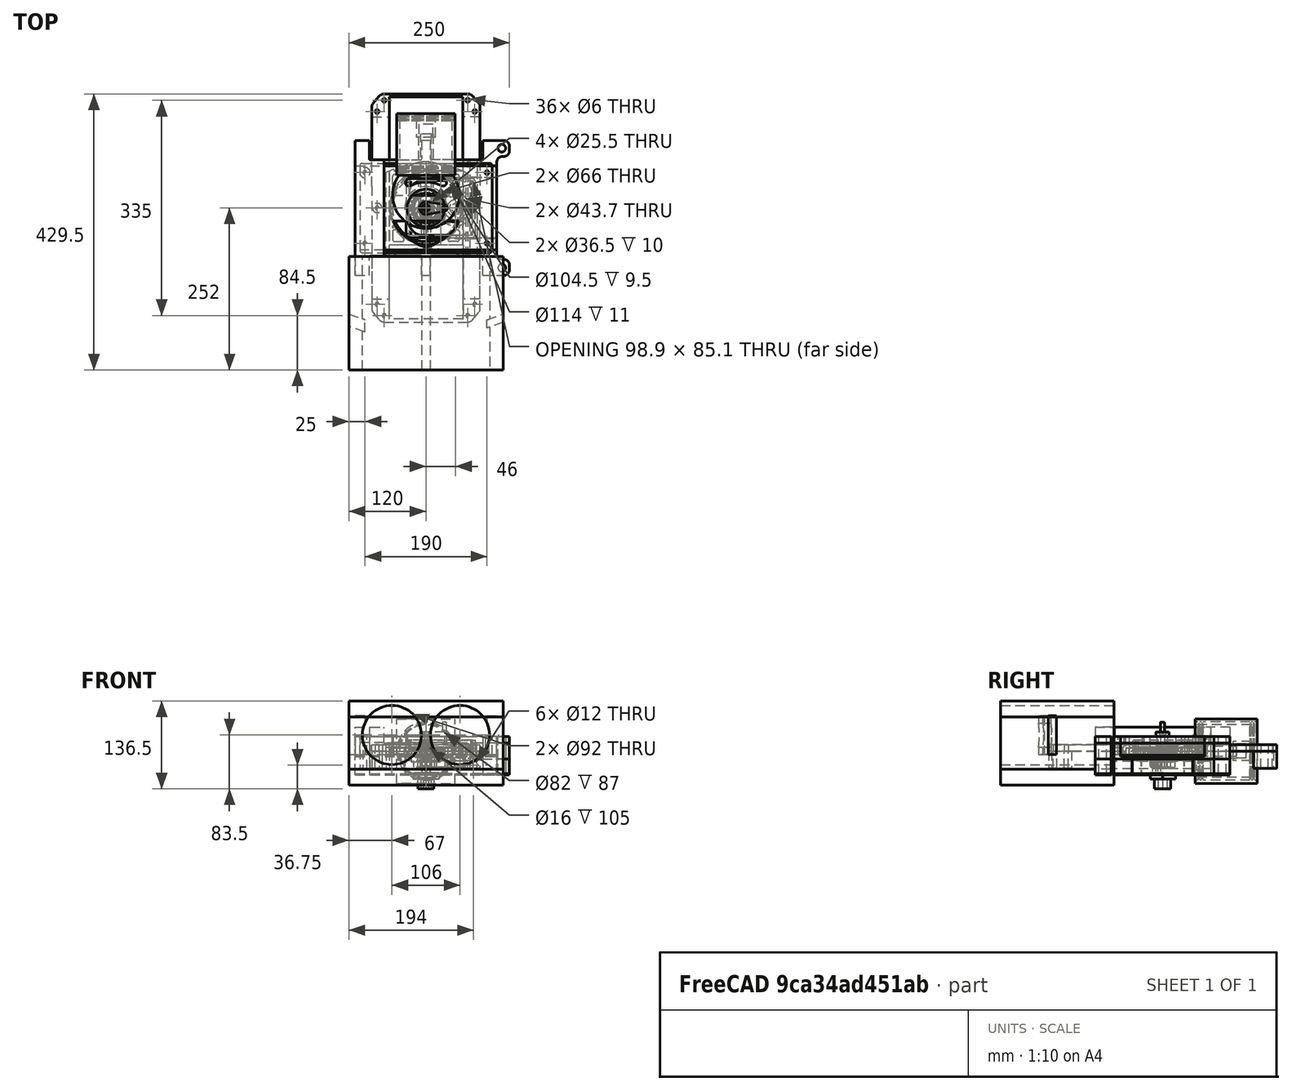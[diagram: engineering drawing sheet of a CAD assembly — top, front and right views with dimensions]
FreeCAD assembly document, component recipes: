
FREECAD ASSEMBLY — COMPONENT RECIPES ("assm4_Paired_at_Tusi_engine")

This assembly document has 39 components, labeled P0..P38 below (a component is one placed body or linked part). 38 of them carry a construction recipe — the FreeCAD feature program that regenerates the part from scratch, quoted from this document or its linked companion documents; the rest are supplied as boundary geometry only. No exploded tour is included for this assembly.
NOTE — document 2 of 2 of this assembly tour. The two overview renders and the header above are repeated from document 1; the component sections below continue where the previous document stopped.
COMPONENT P36 — recipe-attached ("проставка_корпуса_с_шестернями", modeled in this document).
Construction recipe (the document's own serialized feature program — sketch geometry with constraints, then the solid features built on it; lengths are millimeters unless a unit is written):

FEATURE [Sketcher::SketchObject] Sketch075
  FullyConstrained = true
  MapMode = 5
  Support = -> [XY_Plane096]
  expr: Constraints[14] = <<Dim_table>>.inter_shaft_len * 2.15
  expr: Constraints[15] = <<Dim_table>>.ecc_dia * 1.2
  expr: Constraints[16] = <<Dim_table>>.inter_shaft_len * 1.85
  expr: Constraints[22] = <<Dim_table>>.inter_shaft_len / 2
  expr: Constraints[37] = <<Dim_table>>.inter_shaft_len * 2.35
  expr: Constraints[38] = <<Dim_table>>.crank_dia2
  expr: Constraints[39] = <<Dim_table>>.inter_shaft_len * 2
  expr: Constraints[45] = <<Dim_table>>.inter_shaft_len / 2
  expr: Constraints[53] = <<Dim_table>>.axle_hole_dia
  expr: Constraints[56] = <<Dim_table>>.inter_shaft_len
  expr: Constraints[58] = <<Dim_table>>.inter_shaft_len * 0.95
  sketch-geometry (26):
    g0: LineSegment StartX=-4.85 StartY=-42.55 StartZ=0 EndX=50.85 EndY=-42.55 EndZ=0
    g1: LineSegment StartX=72.45 StartY=-20.95 StartZ=0 EndX=72.45 EndY=20.95 EndZ=0
    g2: LineSegment StartX=50.85 StartY=42.55 StartZ=0 EndX=-4.85 EndY=42.55 EndZ=0
    g3: LineSegment StartX=-26.45 StartY=20.95 StartZ=0 EndX=-26.45 EndY=-20.95 EndZ=0
    g4: ArcOfCircle CenterX=-4.85 CenterY=20.95 CenterZ=0 NormalX=0 NormalY=0 NormalZ=1 AngleXU=0 Radius=21.6 StartAngle=1.5708 EndAngle=3.14159
    g5: ArcOfCircle CenterX=50.85 CenterY=20.95 CenterZ=0 NormalX=0 NormalY=0 NormalZ=1 AngleXU=0 Radius=21.6 StartAngle=0 EndAngle=1.5708
    g6: ArcOfCircle CenterX=-4.85 CenterY=-20.95 CenterZ=0 NormalX=0 NormalY=0 NormalZ=1 AngleXU=0 Radius=21.6 StartAngle=3.14159 EndAngle=4.71239
    g7: ArcOfCircle CenterX=50.85 CenterY=-20.95 CenterZ=0 NormalX=0 NormalY=0 NormalZ=1 AngleXU=0 Radius=21.6 StartAngle=4.71239 EndAngle=6.28319
    g8: LineSegment StartX=-26.45 StartY=-20.95 StartZ=0 EndX=72.45 EndY=20.95 EndZ=0
    g9: GeomPoint X=23 Y=0 Z=0
    g10: ArcOfCircle CenterX=-24.8 CenterY=39.75 CenterZ=0 NormalX=0 NormalY=0 NormalZ=1 AngleXU=0 Radius=6.25 StartAngle=1.5708 EndAngle=3.14159
    g11: LineSegment StartX=70.8 StartY=46 StartZ=0 EndX=-24.8 EndY=46 EndZ=0
    g12: ArcOfCircle CenterX=70.8 CenterY=39.75 CenterZ=0 NormalX=0 NormalY=0 NormalZ=1 AngleXU=0 Radius=6.25 StartAngle=0 EndAngle=1.5708
    g13: LineSegment StartX=77.05 StartY=-39.75 StartZ=0 EndX=77.05 EndY=39.75 EndZ=0
    g14: ArcOfCircle CenterX=70.8 CenterY=-39.75 CenterZ=0 NormalX=0 NormalY=0 NormalZ=1 AngleXU=0 Radius=6.25 StartAngle=4.71239 EndAngle=6.28319
    g15: LineSegment StartX=-24.8 StartY=-46 StartZ=0 EndX=70.8 EndY=-46 EndZ=0
    g16: ArcOfCircle CenterX=-24.8 CenterY=-39.75 CenterZ=0 NormalX=0 NormalY=0 NormalZ=1 AngleXU=0 Radius=6.25 StartAngle=3.14159 EndAngle=4.71239
    g17: LineSegment StartX=-31.05 StartY=39.75 StartZ=0 EndX=-31.05 EndY=-39.75 EndZ=0
    g18: LineSegment StartX=-24.8 StartY=46 StartZ=0 EndX=70.8 EndY=-46 EndZ=0
    g19: GeomPoint X=23 Y=0 Z=0
    g20: Circle CenterX=-24.8 CenterY=39.75 CenterZ=0 NormalX=0 NormalY=0 NormalZ=1 AngleXU=0 Radius=1.5
    g21: Circle CenterX=70.8 CenterY=39.75 CenterZ=0 NormalX=0 NormalY=0 NormalZ=1 AngleXU=0 Radius=1.5
    g22: Circle CenterX=-24.8 CenterY=-39.75 CenterZ=0 NormalX=0 NormalY=0 NormalZ=1 AngleXU=0 Radius=1.5
    g23: Circle CenterX=70.8 CenterY=-39.75 CenterZ=0 NormalX=0 NormalY=0 NormalZ=1 AngleXU=0 Radius=1.5
    g24: Circle CenterX=0 CenterY=0 CenterZ=0 NormalX=0 NormalY=0 NormalZ=1 AngleXU=0 Radius=21.85
    g25: Circle CenterX=46 CenterY=0 CenterZ=0 NormalX=0 NormalY=0 NormalZ=1 AngleXU=0 Radius=21.85
  constraints (59):
    c: Horizontal(g0)
    c: Horizontal(g2)
    c: Vertical(g1)
    c: Vertical(g3)
    c: Tangent(g2,g4) = -1.5708
    c: Tangent(g3,g4) = -1.5708
    c: Tangent(g2,g5) = -1.5708
    c: Tangent(g1,g5) = -1.5708
    c: Tangent(g3,g6) = -1.5708
    c: Tangent(g0,g6) = -1.5708
    c: Tangent(g0,g7) = -1.5708
    c: Tangent(g1,g7) = -1.5708
    c: Equal(g4,g5)
    c: Equal(g5,g7)
    c: DistanceX(g3,g1) = 98.9
    c: Diameter(g4) = 43.2
    c: DistanceY(g0,g2) = 85.1
    c: Symmetric(g2,g0,g-1)
    c: Coincident(g8,g3)
    c: Coincident(g8,g1)
    c: PointOnObject(g9,g-1)
    c: PointOnObject(g9,g8)
    c: DistanceX(g-1,g9) = 23
    c: Horizontal(g15)
    c: Horizontal(g11)
    c: Vertical(g13)
    c: Vertical(g17)
    c: Tangent(g11,g10) = -1.5708
    c: Tangent(g17,g10) = -1.5708
    c: Tangent(g11,g12) = -1.5708
    c: Tangent(g13,g12) = -1.5708
    c: Tangent(g17,g16) = -1.5708
    c: Tangent(g15,g16) = -1.5708
    c: Tangent(g15,g14) = -1.5708
    c: Tangent(g13,g14) = -1.5708
    c: Equal(g10,g12)
    c: Equal(g12,g14)
    c: DistanceX(g17,g13) = 108.1
    c: Diameter(g10) = 12.5
    c: DistanceY(g15,g11) = 92
    c: Symmetric(g10,g16,g-1)
    c: Coincident(g18,g10)
    c: Coincident(g18,g14)
    c: PointOnObject(g19,g-1)
    c: PointOnObject(g19,g18)
    c: DistanceX(g-1,g19) = 23
    c: Coincident(g20,g10)
    c: Coincident(g21,g12)
    c: Coincident(g22,g16)
    c: Coincident(g23,g14)
    c: Equal(g22,g23)
    c: Equal(g23,g21)
    c: Equal(g21,g20)
    c: Diameter(g20) = 3
    c: Coincident(g24,g-1)
    c: PointOnObject(g25,g-1)
    c: DistanceX(g24,g25) = 46
    c: Equal(g25,g24)
    c: Diameter(g24) = 43.7
FEATURE [Sketcher::SketchObject] Sketch076
  FullyConstrained = true
  MapMode = 5
  Support = -> [XY_Plane096]
  expr: Constraints[14] = <<Dim_table>>.inter_shaft_len * 2.15
  expr: Constraints[15] = <<Dim_table>>.ecc_dia * 1.2
  expr: Constraints[16] = <<Dim_table>>.inter_shaft_len * 1.85
  expr: Constraints[22] = <<Dim_table>>.inter_shaft_len / 2
  expr: Constraints[37] = <<Dim_table>>.inter_shaft_len * 2.35
  expr: Constraints[38] = <<Dim_table>>.crank_dia2
  expr: Constraints[39] = <<Dim_table>>.inter_shaft_len * 2
  expr: Constraints[45] = <<Dim_table>>.inter_shaft_len / 2
  expr: Constraints[53] = <<Dim_table>>.axle_hole_dia
  sketch-geometry (24):
    g0: LineSegment StartX=-4.85 StartY=-42.55 StartZ=0 EndX=50.85 EndY=-42.55 EndZ=0
    g1: LineSegment StartX=72.45 StartY=-20.95 StartZ=0 EndX=72.45 EndY=20.95 EndZ=0
    g2: LineSegment StartX=50.85 StartY=42.55 StartZ=0 EndX=-4.85 EndY=42.55 EndZ=0
    g3: LineSegment StartX=-26.45 StartY=20.95 StartZ=0 EndX=-26.45 EndY=-20.95 EndZ=0
    g4: ArcOfCircle CenterX=-4.85 CenterY=20.95 CenterZ=0 NormalX=0 NormalY=0 NormalZ=1 AngleXU=0 Radius=21.6 StartAngle=1.5708 EndAngle=3.14159
    g5: ArcOfCircle CenterX=50.85 CenterY=20.95 CenterZ=0 NormalX=0 NormalY=0 NormalZ=1 AngleXU=0 Radius=21.6 StartAngle=0 EndAngle=1.5708
    g6: ArcOfCircle CenterX=-4.85 CenterY=-20.95 CenterZ=0 NormalX=0 NormalY=0 NormalZ=1 AngleXU=0 Radius=21.6 StartAngle=3.14159 EndAngle=4.71239
    g7: ArcOfCircle CenterX=50.85 CenterY=-20.95 CenterZ=0 NormalX=0 NormalY=0 NormalZ=1 AngleXU=0 Radius=21.6 StartAngle=4.71239 EndAngle=6.28319
    g8: LineSegment StartX=-26.45 StartY=-20.95 StartZ=0 EndX=72.45 EndY=20.95 EndZ=0
    g9: GeomPoint X=23 Y=0 Z=0
    g10: ArcOfCircle CenterX=-24.8 CenterY=39.75 CenterZ=0 NormalX=0 NormalY=0 NormalZ=1 AngleXU=0 Radius=6.25 StartAngle=1.5708 EndAngle=3.14159
    g11: LineSegment StartX=70.8 StartY=46 StartZ=0 EndX=-24.8 EndY=46 EndZ=0
    g12: ArcOfCircle CenterX=70.8 CenterY=39.75 CenterZ=0 NormalX=0 NormalY=0 NormalZ=1 AngleXU=0 Radius=6.25 StartAngle=0 EndAngle=1.5708
    g13: LineSegment StartX=77.05 StartY=-39.75 StartZ=0 EndX=77.05 EndY=39.75 EndZ=0
    g14: ArcOfCircle CenterX=70.8 CenterY=-39.75 CenterZ=0 NormalX=0 NormalY=0 NormalZ=1 AngleXU=0 Radius=6.25 StartAngle=4.71239 EndAngle=6.28319
    g15: LineSegment StartX=-24.8 StartY=-46 StartZ=0 EndX=70.8 EndY=-46 EndZ=0
    g16: ArcOfCircle CenterX=-24.8 CenterY=-39.75 CenterZ=0 NormalX=0 NormalY=0 NormalZ=1 AngleXU=0 Radius=6.25 StartAngle=3.14159 EndAngle=4.71239
    g17: LineSegment StartX=-31.05 StartY=39.75 StartZ=0 EndX=-31.05 EndY=-39.75 EndZ=0
    g18: LineSegment StartX=-24.8 StartY=46 StartZ=0 EndX=70.8 EndY=-46 EndZ=0
    g19: GeomPoint X=23 Y=0 Z=0
    g20: Circle CenterX=-24.8 CenterY=39.75 CenterZ=0 NormalX=0 NormalY=0 NormalZ=1 AngleXU=0 Radius=1.5
    g21: Circle CenterX=70.8 CenterY=39.75 CenterZ=0 NormalX=0 NormalY=0 NormalZ=1 AngleXU=0 Radius=1.5
    g22: Circle CenterX=-24.8 CenterY=-39.75 CenterZ=0 NormalX=0 NormalY=0 NormalZ=1 AngleXU=0 Radius=1.5
    g23: Circle CenterX=70.8 CenterY=-39.75 CenterZ=0 NormalX=0 NormalY=0 NormalZ=1 AngleXU=0 Radius=1.5
  constraints (54):
    c: Horizontal(g0)
    c: Horizontal(g2)
    c: Vertical(g1)
    c: Vertical(g3)
    c: Tangent(g2,g4) = -1.5708
    c: Tangent(g3,g4) = -1.5708
    c: Tangent(g2,g5) = -1.5708
    c: Tangent(g1,g5) = -1.5708
    c: Tangent(g3,g6) = -1.5708
    c: Tangent(g0,g6) = -1.5708
    c: Tangent(g0,g7) = -1.5708
    c: Tangent(g1,g7) = -1.5708
    c: Equal(g4,g5)
    c: Equal(g5,g7)
    c: DistanceX(g3,g1) = 98.9
    c: Diameter(g4) = 43.2
    c: DistanceY(g0,g2) = 85.1
    c: Symmetric(g2,g0,g-1)
    c: Coincident(g8,g3)
    c: Coincident(g8,g1)
    c: PointOnObject(g9,g-1)
    c: PointOnObject(g9,g8)
    c: DistanceX(g-1,g9) = 23
    c: Horizontal(g15)
    c: Horizontal(g11)
    c: Vertical(g13)
    c: Vertical(g17)
    c: Tangent(g11,g10) = -1.5708
    c: Tangent(g17,g10) = -1.5708
    c: Tangent(g11,g12) = -1.5708
    c: Tangent(g13,g12) = -1.5708
    c: Tangent(g17,g16) = -1.5708
    c: Tangent(g15,g16) = -1.5708
    c: Tangent(g15,g14) = -1.5708
    c: Tangent(g13,g14) = -1.5708
    c: Equal(g10,g12)
    c: Equal(g12,g14)
    c: DistanceX(g17,g13) = 108.1
    c: Diameter(g10) = 12.5
    c: DistanceY(g15,g11) = 92
    c: Symmetric(g10,g16,g-1)
    c: Coincident(g18,g10)
    c: Coincident(g18,g14)
    c: PointOnObject(g19,g-1)
    c: PointOnObject(g19,g18)
    c: DistanceX(g-1,g19) = 23
    c: Coincident(g20,g10)
    c: Coincident(g21,g12)
    c: Coincident(g22,g16)
    c: Coincident(g23,g14)
    c: Equal(g22,g23)
    c: Equal(g23,g21)
    c: Equal(g21,g20)
    c: Diameter(g20) = 3
FEATURE [PartDesign::CoordinateSystem] LCS_Origin007
  AttacherType = Attacher::AttachEngine3D
  MapMode = 2
  Support = -> [X_Axis094]
FEATURE [PartDesign::Pad] Pad044
  Direction = (0,0,1)
  Length = 6
  Length2 = 10
  Profile = -> Sketch075
  ReferenceAxis = -> Sketch075 [N_Axis]
  Type = 0
FEATURE [PartDesign::Pad] Pad045
  BaseFeature = -> Pad044
  Direction = (0,0,1)
  Length = 16.75
  Length2 = 10
  Profile = -> Sketch076
  ReferenceAxis = -> Sketch076 [N_Axis]
  Type = 0
FEATURE [PartDesign::Body] Body_2  label="проставка_корпуса_с_шестернями"
  Group = -> [LCS_Origin007,Sketch075,Pad044,Sketch076,Pad045]
  Origin = -> Origin095
  Tip = -> Pad045
COMPONENT P37 — recipe-attached ("направляющая_нижнего ползуна", modeled in this document).
Construction recipe (the document's own serialized feature program — sketch geometry with constraints, then the solid features built on it; lengths are millimeters unless a unit is written):

FEATURE [Sketcher::SketchObject] Sketch065
  FullyConstrained = false
  MapMode = 5
  Support = -> [XY_Plane083]
  expr: Constraints[34] = <<assm4_Main_BSM_M3_r80>>#<<Dim_table>>.inter_shaft_len
  expr: Constraints[80] = <<assm4_Main_BSM_M3_r80>>#<<Dim_table>>.ecc_dia + 10 + 0.5
  sketch-geometry (37):
    g0: LineSegment StartX=-84 StartY=-33.8723 StartZ=0 EndX=84 EndY=-33.8723 EndZ=0
    g1: LineSegment StartX=84 StartY=-33.8723 StartZ=0 EndX=84 EndY=33.8723 EndZ=0
    g2: LineSegment StartX=84 StartY=33.8723 StartZ=0 EndX=-84 EndY=33.8723 EndZ=0
    g3: LineSegment StartX=-84 StartY=33.8723 StartZ=0 EndX=-84 EndY=-33.8723 EndZ=0
    g4: LineSegment StartX=-84 StartY=33.8723 StartZ=0 EndX=-84 EndY=159.195 EndZ=0
    g5: LineSegment StartX=84 StartY=159.195 StartZ=0 EndX=84 EndY=33.8723 EndZ=0
    g6: ArcOfCircle CenterX=-80 CenterY=159.195 CenterZ=0 NormalX=0 NormalY=0 NormalZ=1 AngleXU=0 Radius=4 StartAngle=2.43396 EndAngle=3.14159
    g7: ArcOfCircle CenterX=80 CenterY=159.195 CenterZ=0 NormalX=0 NormalY=0 NormalZ=1 AngleXU=0 Radius=4 StartAngle=-2.7e-13 EndAngle=0.707637
    g8: LineSegment StartX=-84 StartY=-33.8723 StartZ=0 EndX=-84 EndY=-159.195 EndZ=0
    g9: LineSegment StartX=84 StartY=-159.195 StartZ=0 EndX=84 EndY=-33.8723 EndZ=0
    g10: Circle CenterX=-76 CenterY=150 CenterZ=0 NormalX=0 NormalY=0 NormalZ=1 AngleXU=0 Radius=3
    g11: Circle CenterX=76 CenterY=150 CenterZ=0 NormalX=0 NormalY=0 NormalZ=1 AngleXU=0 Radius=3
    g12: Circle CenterX=-76 CenterY=-150 CenterZ=0 NormalX=0 NormalY=0 NormalZ=1 AngleXU=0 Radius=3
    g13: Circle CenterX=76 CenterY=-150 CenterZ=0 NormalX=0 NormalY=0 NormalZ=1 AngleXU=0 Radius=3
    g14: Circle CenterX=76 CenterY=0 CenterZ=0 NormalX=0 NormalY=0 NormalZ=1 AngleXU=0 Radius=3
    g15: Circle CenterX=-76 CenterY=0 CenterZ=0 NormalX=0 NormalY=0 NormalZ=1 AngleXU=0 Radius=3
    g16: LineSegment StartX=-65 StartY=177.5 StartZ=0 EndX=65 EndY=177.5 EndZ=0
    g17: LineSegment StartX=72.599 StartY=174 StartZ=0 EndX=83.0396 EndY=161.795 EndZ=0
    g18: LineSegment StartX=-83.0396 StartY=161.795 StartZ=0 EndX=-72.599 EndY=174 EndZ=0
    g19: ArcOfCircle CenterX=-65 CenterY=167.5 CenterZ=0 NormalX=0 NormalY=0 NormalZ=1 AngleXU=0 Radius=10 StartAngle=1.5708 EndAngle=2.43396
    g20: ArcOfCircle CenterX=65 CenterY=167.5 CenterZ=0 NormalX=0 NormalY=0 NormalZ=1 AngleXU=0 Radius=10 StartAngle=0.707637 EndAngle=1.5708
    g21: ArcOfCircle CenterX=-80 CenterY=-159.195 CenterZ=0 NormalX=0 NormalY=0 NormalZ=1 AngleXU=0 Radius=4 StartAngle=3.14159 EndAngle=3.84923
    g22: ArcOfCircle CenterX=80 CenterY=-159.195 CenterZ=0 NormalX=0 NormalY=0 NormalZ=1 AngleXU=0 Radius=4 StartAngle=5.57555 EndAngle=6.28319
    g23: LineSegment StartX=-65 StartY=-177.5 StartZ=0 EndX=65 EndY=-177.5 EndZ=0
    g24: LineSegment StartX=72.599 StartY=-174 StartZ=0 EndX=83.0396 EndY=-161.795 EndZ=0
    g25: LineSegment StartX=-83.0396 StartY=-161.795 StartZ=0 EndX=-72.599 EndY=-174 EndZ=0
    g26: ArcOfCircle CenterX=-65 CenterY=-167.5 CenterZ=0 NormalX=0 NormalY=0 NormalZ=1 AngleXU=0 Radius=10 StartAngle=3.84923 EndAngle=4.71239
    g27: ArcOfCircle CenterX=65 CenterY=-167.5 CenterZ=0 NormalX=0 NormalY=0 NormalZ=1 AngleXU=0 Radius=10 StartAngle=4.71239 EndAngle=5.57555
    g28: Circle CenterX=-65 CenterY=167.5 CenterZ=0 NormalX=0 NormalY=0 NormalZ=1 AngleXU=0 Radius=3
    g29: Circle CenterX=65 CenterY=167.5 CenterZ=0 NormalX=0 NormalY=0 NormalZ=1 AngleXU=0 Radius=3
    g30: Circle CenterX=-65 CenterY=-167.5 CenterZ=0 NormalX=0 NormalY=0 NormalZ=1 AngleXU=0 Radius=3
    g31: Circle CenterX=65 CenterY=-167.5 CenterZ=0 NormalX=0 NormalY=0 NormalZ=1 AngleXU=0 Radius=3
    g32: LineSegment StartX=57.25 StartY=-172.5 StartZ=0 EndX=-57.25 EndY=-172.5 EndZ=0
    g33: LineSegment StartX=-57.25 StartY=-172.5 StartZ=0 EndX=-57.25 EndY=172.5 EndZ=0
    g34: LineSegment StartX=-57.25 StartY=172.5 StartZ=0 EndX=57.25 EndY=172.5 EndZ=0
    g35: LineSegment StartX=57.25 StartY=172.5 StartZ=0 EndX=57.25 EndY=-172.5 EndZ=0
    g36: LineSegment StartX=57.25 StartY=-172.5 StartZ=0 EndX=-57.25 EndY=172.5 EndZ=0
  constraints (82):
    c: Coincident(g0,g1)
    c: Coincident(g1,g2)
    c: Coincident(g2,g3)
    c: Coincident(g3,g0)
    c: Horizontal(g0)
    c: Vertical(g1)
    c: Symmetric(g2,g1,g-2)
    c: Symmetric(g2,g0,g-1)
    c: DistanceX(g2,g2) = 168
    c: Coincident(g4,g3)
    c: Coincident(g5,g1)
    c: Tangent(g4,g6) = 1.5708
    c: Tangent(g5,g7) = 1.5708
    c: Vertical(g4)
    c: Vertical(g5)
    c: Symmetric(g6,g7,g-2)
    c: Radius(g7) = 4
    c: Vertical(g8)
    c: Coincident(g8,g3)
    c: Coincident(g9,g1)
    c: Vertical(g9)
    c: Equal(g10,g11)
    c: Equal(g11,g13)
    c: Equal(g13,g12)
    c: Diameter(g11) = 6
    c: Symmetric(g10,g11,g-2)
    c: Symmetric(g12,g13,g-2)
    c: Symmetric(g12,g10,g-1)
    c: DistanceX(g3,g10) = 8
    c: Equal(g15,g14)
    c: Symmetric(g15,g14,g-2)
    c: PointOnObject(g14,g-1)
    c: DistanceX(g12,g15) = 0
    c: Equal(g15,g10)
    c: DistanceY(g15,g10) = 150
    c: Horizontal(g16)
    c: Tangent(g6,g18) = 1.5708
    c: Tangent(g18,g19) = 1.5708
    c: Tangent(g16,g19) = 1.5708
    c: Tangent(g16,g20) = 1.5708
    c: Tangent(g17,g20) = 1.5708
    c: Tangent(g17,g7) = 1.5708
    c: Symmetric(g19,g20,g-2)
    c: Radius(g22) = 4
    c: Horizontal(g23)
    c: Tangent(g21,g25) = -1.5708
    c: Tangent(g25,g26) = -1.5708
    c: Tangent(g23,g26) = -1.5708
    c: Tangent(g23,g27) = -1.5708
    c: Tangent(g24,g27) = -1.5708
    c: Tangent(g24,g22) = -1.5708
    c: Equal(g25,g18)
    c: Symmetric(g26,g27,g-2)
    c: Equal(g26,g19)
    c: Tangent(g21,g8) = -1.5708
    c: Tangent(g22,g9) = -1.5708
    c: Symmetric(g21,g22,g-2)
    c: DistanceY(g23,g16) = 355
    c: Coincident(g28,g19)
    c: Coincident(g29,g20)
    c: Equal(g28,g29)
    c: Equal(g29,g10)
    c: Equal(g30,g31)
    c: Coincident(g30,g26)
    c: Coincident(g31,g27)
    c: Equal(g31,g13)
    c: DistanceX(g26,g27) = 130
    c: DistanceY(g27,g20) = 335
    c: Symmetric(g16,g23,g-1)
    c: Coincident(g32,g33)
    c: Coincident(g33,g34)
    c: Coincident(g34,g35)
    c: Coincident(g35,g32)
    c: Horizontal(g32)
    c: Horizontal(g34)
    c: Vertical(g33)
    c: Vertical(g35)
    c: Coincident(g36,g32)
    c: Coincident(g36,g33)
    c: Symmetric(g32,g33,g-1)
    c: Distance(g34) = 114.5
    c: DistanceY(g34,g16) = 5
FEATURE [PartDesign::CoordinateSystem] LCS_Origin005
  AttacherType = Attacher::AttachEngine3D
  MapMode = 2
  Support = -> [X_Axis081]
FEATURE [PartDesign::Pad] Pad035
  Direction = (0,0,1)
  Length = 10
  Length2 = 10
  Profile = -> Sketch065
  ReferenceAxis = -> Sketch065 [N_Axis]
  Type = 0
FEATURE [Sketcher::SketchObject] Sketch068
  ExternalGeometry = -> [Pad035]
  FullyConstrained = true
  MapMode = 5
  Placement = pos=(0,-172.5,0) rot=(0,0.707107,0.707107;3.14159rad)
  Support = -> [Pad035]
  sketch-geometry (4):
    g0: ArcOfCircle CenterX=-37.8851 CenterY=5 CenterZ=0 NormalX=0 NormalY=0 NormalZ=1 AngleXU=0 Radius=20 StartAngle=2.88891 EndAngle=3.39427
    g1: ArcOfCircle CenterX=37.8851 CenterY=5 CenterZ=0 NormalX=0 NormalY=0 NormalZ=1 AngleXU=0 Radius=20 StartAngle=6.03051 EndAngle=6.53587
    g2: LineSegment StartX=-57.25 StartY=10 StartZ=0 EndX=-57.25 EndY=1.8296e-12 EndZ=0
    g3: LineSegment StartX=57.25 StartY=10 StartZ=0 EndX=57.25 EndY=1.8243e-12 EndZ=0
  constraints (10):
    c: Coincident(g0,g-3)
    c: Coincident(g0,g-3)
    c: Coincident(g1,g-4)
    c: Coincident(g1,g-4)
    c: Equal(g0,g1)
    c: Radius(g1) = 20
    c: Coincident(g2,g0)
    c: Coincident(g2,g0)
    c: Coincident(g3,g1)
    c: Coincident(g3,g1)
FEATURE [PartDesign::Pocket] Pocket035
  BaseFeature = -> Pad035
  Direction = (0,-1,2e-16)
  Length = 345
  Length2 = 5
  Profile = -> Sketch068
  ReferenceAxis = -> Sketch068 [N_Axis]
  Reversed = true
  Type = 0
FEATURE [PartDesign::Body] ________________________  label="направляющая_нижнего ползуна"
  Group = -> [LCS_Origin005,Sketch065,Pad035,Sketch068,Pocket035]
  Origin = -> Origin082
  Tip = -> Pocket035
COMPONENT P38 — recipe-attached ("корпус_верхний", modeled in this document).
Construction recipe (the document's own serialized feature program — sketch geometry with constraints, then the solid features built on it; lengths are millimeters unless a unit is written):

FEATURE [Sketcher::SketchObject] Sketch067
  FullyConstrained = true
  MapMode = 5
  Support = -> [XY_Plane085]
  expr: Constraints[14] = <<Dim_table>>.inter_shaft_len * 2.15
  expr: Constraints[15] = <<Dim_table>>.ecc_dia * 1.2
  expr: Constraints[16] = <<Dim_table>>.inter_shaft_len * 1.85
  expr: Constraints[22] = <<Dim_table>>.inter_shaft_len / 2
  expr: Constraints[37] = <<Dim_table>>.inter_shaft_len * 2.35
  expr: Constraints[38] = <<Dim_table>>.crank_dia2
  expr: Constraints[39] = <<Dim_table>>.inter_shaft_len * 2
  expr: Constraints[45] = <<Dim_table>>.inter_shaft_len / 2
  expr: Constraints[53] = <<Dim_table>>.axle_hole_dia
  expr: Constraints[56] = <<Dim_table>>.inter_shaft_len
  expr: Constraints[58] = <<Dim_table>>.crank_dia2 + <<Dim_table>>.zazor
  sketch-geometry (27):
    g0: LineSegment StartX=-4.85 StartY=-42.55 StartZ=0 EndX=50.85 EndY=-42.55 EndZ=0
    g1: LineSegment StartX=72.45 StartY=-20.95 StartZ=0 EndX=72.45 EndY=20.95 EndZ=0
    g2: LineSegment StartX=50.85 StartY=42.55 StartZ=0 EndX=-4.85 EndY=42.55 EndZ=0
    g3: LineSegment StartX=-26.45 StartY=20.95 StartZ=0 EndX=-26.45 EndY=-20.95 EndZ=0
    g4: ArcOfCircle CenterX=-4.85 CenterY=20.95 CenterZ=0 NormalX=0 NormalY=0 NormalZ=1 AngleXU=0 Radius=21.6 StartAngle=1.5708 EndAngle=3.14159
    g5: ArcOfCircle CenterX=50.85 CenterY=20.95 CenterZ=0 NormalX=0 NormalY=0 NormalZ=1 AngleXU=0 Radius=21.6 StartAngle=0 EndAngle=1.5708
    g6: ArcOfCircle CenterX=-4.85 CenterY=-20.95 CenterZ=0 NormalX=0 NormalY=0 NormalZ=1 AngleXU=0 Radius=21.6 StartAngle=3.14159 EndAngle=4.71239
    g7: ArcOfCircle CenterX=50.85 CenterY=-20.95 CenterZ=0 NormalX=0 NormalY=0 NormalZ=1 AngleXU=0 Radius=21.6 StartAngle=4.71239 EndAngle=6.28319
    g8: LineSegment StartX=-26.45 StartY=-20.95 StartZ=0 EndX=72.45 EndY=20.95 EndZ=0
    g9: GeomPoint X=23 Y=0 Z=0
    g10: ArcOfCircle CenterX=-24.8 CenterY=39.75 CenterZ=0 NormalX=0 NormalY=0 NormalZ=1 AngleXU=0 Radius=6.25 StartAngle=1.5708 EndAngle=3.14159
    g11: LineSegment StartX=70.8 StartY=46 StartZ=0 EndX=-24.8 EndY=46 EndZ=0
    g12: ArcOfCircle CenterX=70.8 CenterY=39.75 CenterZ=0 NormalX=0 NormalY=0 NormalZ=1 AngleXU=0 Radius=6.25 StartAngle=0 EndAngle=1.5708
    g13: LineSegment StartX=77.05 StartY=-39.75 StartZ=0 EndX=77.05 EndY=39.75 EndZ=0
    g14: ArcOfCircle CenterX=70.8 CenterY=-39.75 CenterZ=0 NormalX=0 NormalY=0 NormalZ=1 AngleXU=0 Radius=6.25 StartAngle=4.71239 EndAngle=6.28319
    g15: LineSegment StartX=-24.8 StartY=-46 StartZ=0 EndX=70.8 EndY=-46 EndZ=0
    g16: ArcOfCircle CenterX=-24.8 CenterY=-39.75 CenterZ=0 NormalX=0 NormalY=0 NormalZ=1 AngleXU=0 Radius=6.25 StartAngle=3.14159 EndAngle=4.71239
    g17: LineSegment StartX=-31.05 StartY=39.75 StartZ=0 EndX=-31.05 EndY=-39.75 EndZ=0
    g18: LineSegment StartX=-24.8 StartY=46 StartZ=0 EndX=70.8 EndY=-46 EndZ=0
    g19: GeomPoint X=23 Y=0 Z=0
    g20: Circle CenterX=-24.8 CenterY=39.75 CenterZ=0 NormalX=0 NormalY=0 NormalZ=1 AngleXU=0 Radius=1.5
    g21: Circle CenterX=70.8 CenterY=39.75 CenterZ=0 NormalX=0 NormalY=0 NormalZ=1 AngleXU=0 Radius=1.5
    g22: Circle CenterX=-24.8 CenterY=-39.75 CenterZ=0 NormalX=0 NormalY=0 NormalZ=1 AngleXU=0 Radius=1.5
    g23: Circle CenterX=70.8 CenterY=-39.75 CenterZ=0 NormalX=0 NormalY=0 NormalZ=1 AngleXU=0 Radius=1.5
    g24: Circle CenterX=0 CenterY=0 CenterZ=0 NormalX=0 NormalY=0 NormalZ=1 AngleXU=0 Radius=6.5
    g25: Circle CenterX=46 CenterY=0 CenterZ=0 NormalX=0 NormalY=0 NormalZ=1 AngleXU=0 Radius=6.5
    g26: Circle CenterX=23 CenterY=0 CenterZ=0 NormalX=0 NormalY=0 NormalZ=1 AngleXU=0 Radius=6.5
  constraints (61):
    c: Horizontal(g0)
    c: Horizontal(g2)
    c: Vertical(g1)
    c: Vertical(g3)
    c: Tangent(g2,g4) = -1.5708
    c: Tangent(g3,g4) = -1.5708
    c: Tangent(g2,g5) = -1.5708
    c: Tangent(g1,g5) = -1.5708
    c: Tangent(g3,g6) = -1.5708
    c: Tangent(g0,g6) = -1.5708
    c: Tangent(g0,g7) = -1.5708
    c: Tangent(g1,g7) = -1.5708
    c: Equal(g4,g5)
    c: Equal(g5,g7)
    c: DistanceX(g3,g1) = 98.9
    c: Diameter(g4) = 43.2
    c: DistanceY(g0,g2) = 85.1
    c: Symmetric(g2,g0,g-1)
    c: Coincident(g8,g3)
    c: Coincident(g8,g1)
    c: PointOnObject(g9,g-1)
    c: PointOnObject(g9,g8)
    c: DistanceX(g-1,g9) = 23
    c: Horizontal(g15)
    c: Horizontal(g11)
    c: Vertical(g13)
    c: Vertical(g17)
    c: Tangent(g11,g10) = -1.5708
    c: Tangent(g17,g10) = -1.5708
    c: Tangent(g11,g12) = -1.5708
    c: Tangent(g13,g12) = -1.5708
    c: Tangent(g17,g16) = -1.5708
    c: Tangent(g15,g16) = -1.5708
    c: Tangent(g15,g14) = -1.5708
    c: Tangent(g13,g14) = -1.5708
    c: Equal(g10,g12)
    c: Equal(g12,g14)
    c: DistanceX(g17,g13) = 108.1
    c: Diameter(g10) = 12.5
    c: DistanceY(g15,g11) = 92
    c: Symmetric(g10,g16,g-1)
    c: Coincident(g18,g10)
    c: Coincident(g18,g14)
    c: PointOnObject(g19,g-1)
    c: PointOnObject(g19,g18)
    c: DistanceX(g-1,g19) = 23
    c: Coincident(g20,g10)
    c: Coincident(g21,g12)
    c: Coincident(g22,g16)
    c: Coincident(g23,g14)
    c: Equal(g22,g23)
    c: Equal(g23,g21)
    c: Equal(g21,g20)
    c: Diameter(g20) = 3
    c: Coincident(g24,g-1)
    c: PointOnObject(g25,g-1)
    c: DistanceX(g24,g25) = 46
    c: Equal(g25,g24)
    c: Diameter(g24) = 13
    c: Coincident(g26,g9)
    c: Equal(g24,g26)
FEATURE [PartDesign::CoordinateSystem] LCS_Origin006
  AttacherType = Attacher::AttachEngine3D
  MapMode = 2
  Support = -> [X_Axis083]
FEATURE [PartDesign::Pad] Pad036
  Direction = (0,0,1)
  Length = 4
  Length2 = 10
  Profile = -> Sketch067
  ReferenceAxis = -> Sketch067 [N_Axis]
  Type = 0
FEATURE [Sketcher::SketchObject] Sketch073
  FullyConstrained = true
  MapMode = 5
  Support = -> [XY_Plane085]
  expr: Constraints[6] = <<Dim_table>>.crank_dia2 + <<Dim_table>>.zazor
  expr: Constraints[7] = <<Dim_table>>.crank_dia2 * 1.5
  expr: Constraints[8] = <<Dim_table>>.inter_shaft_len
  sketch-geometry (4):
    g0: Circle CenterX=0 CenterY=0 CenterZ=0 NormalX=0 NormalY=0 NormalZ=1 AngleXU=0 Radius=6.5
    g1: Circle CenterX=0 CenterY=0 CenterZ=0 NormalX=0 NormalY=0 NormalZ=1 AngleXU=0 Radius=9.375
    g2: Circle CenterX=46 CenterY=0 CenterZ=0 NormalX=0 NormalY=0 NormalZ=1 AngleXU=0 Radius=6.5
    g3: Circle CenterX=46 CenterY=0 CenterZ=0 NormalX=0 NormalY=0 NormalZ=1 AngleXU=0 Radius=9.375
  constraints (9):
    c: Coincident(g0,g-1)
    c: Coincident(g1,g0)
    c: PointOnObject(g2,g-1)
    c: Coincident(g3,g2)
    c: Equal(g0,g2)
    c: Equal(g1,g3)
    c: Diameter(g0) = 13
    c: Diameter(g1) = 18.75
    c: DistanceX(g-1,g2) = 46
FEATURE [PartDesign::Pad] Pad041
  BaseFeature = -> Pad036
  Direction = (0,0,1)
  Length = 10
  Length2 = 10
  Profile = -> Sketch073
  ReferenceAxis = -> Sketch073 [N_Axis]
  Type = 0
FEATURE [PartDesign::Body] ___________________________  label="корпус_верхний"
  Group = -> [LCS_Origin006,Sketch067,Pad036,Sketch073,Pad041]
  Origin = -> Origin084
  Tip = -> Pad041
PROVENANCE & LICENSES
A FreeCAD (.FCStd) document from a public repository crawl; recipes are the document's own serialized feature recipes (and, for linked parts, companion documents' recipes).
License: unknown-license-file.
